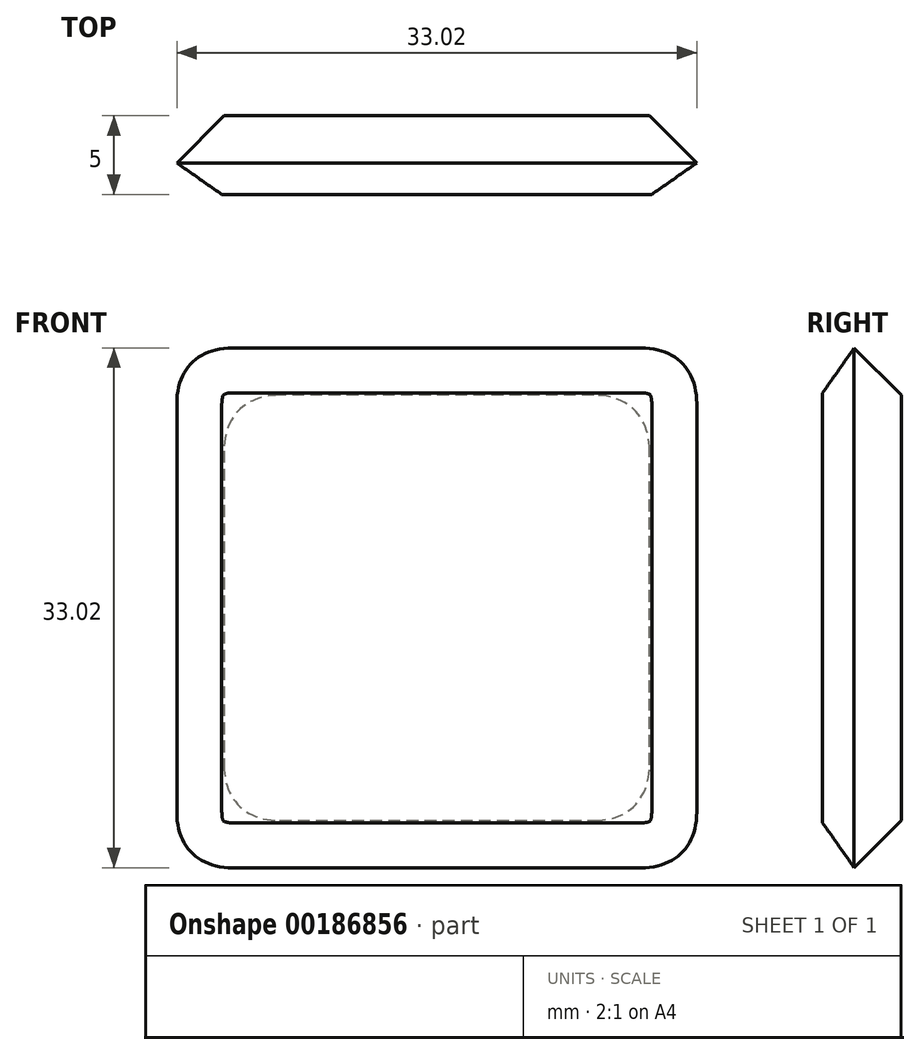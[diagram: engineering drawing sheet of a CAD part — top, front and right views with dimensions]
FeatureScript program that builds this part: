
annotation { "Feature Type Name" : "Feature", "Feature Type Description" : "" }
export const myFeature = defineFeature(function(context is Context, id is Id, definition is map)
    precondition{}
    {
        {
            var Q0;
            Q0=qCreatedBy(makeId("Front.planeOp"),FACE);
            var sketch = newSketch(context, id + "F0", { "sketchPlane" : qUnion([Q0])});
            skLineSegment(sketch, "E0.bottom", {"start": v(-16.51, 16.51) * mm, "end": v(16.51, 16.51) * mm});
            skLineSegment(sketch, "E0.top", {"start": v(-16.51, -16.51) * mm, "end": v(16.51, -16.51) * mm});
            skLineSegment(sketch, "E0.left", {"start": v(-16.51, 16.51) * mm, "end": v(-16.51, -16.51) * mm});
            skLineSegment(sketch, "E0.right", {"start": v(16.51, 16.51) * mm, "end": v(16.51, -16.51) * mm});
            skPoint(sketch, "E0.middle", {"position": v(0, 0) * mm});
            skSolve(sketch);
        }
        {
            var Q0;
            Q0=makeQuery(id+"F0.imprint","IMPRINT",FACE,{"disambiguationData":[TD([[makeQuery(id+"F0.imprint","IMPRINT",EDGE,{"derivedFrom":sQuery(id+"F0.wireOp",EDGE,"E0.bottom")}),-1.0]])]});
            extrude(context, id + "F1", {"entities" : qUnion([Q0]), "oppositeDirection" : true, "depth" : 3 * mm, "hasDraft" : true, "draftAngle" : 45 * degree, "draftPullDirection" : true});
        }
        {
            var Q0;
            Q0=makeQuery(id+"F1.opExtrude","SWEPT_EDGE",EDGE,{"disambiguationData":[OSD([sQuery(id+"F0.wireOp",EDGE,"E0.top"),sQuery(id+"F0.wireOp",EDGE,"E0.left")])]});
            var Q1;
            Q1=makeQuery(id+"F1.opExtrude","SWEPT_EDGE",EDGE,{"disambiguationData":[OSD([sQuery(id+"F0.wireOp",EDGE,"E0.bottom"),sQuery(id+"F0.wireOp",EDGE,"E0.left")])]});
            var Q2;
            Q2=makeQuery(id+"F1.opExtrude","SWEPT_EDGE",EDGE,{"disambiguationData":[OSD([sQuery(id+"F0.wireOp",EDGE,"E0.bottom"),sQuery(id+"F0.wireOp",EDGE,"E0.right")])]});
            var Q3;
            Q3=makeQuery(id+"F1.opExtrude","SWEPT_EDGE",EDGE,{"disambiguationData":[OSD([sQuery(id+"F0.wireOp",EDGE,"E0.top"),sQuery(id+"F0.wireOp",EDGE,"E0.right")])]});
            fillet(context, id + "F2", {"entities" : qUnion([Q0, Q1, Q2, Q3]), "radius" : 5 * mm, "tangentPropagation" : true, "allowEdgeOverflow" : false});
        }
        {
            var Q0;
            Q0=makeQuery(id+"F1.opExtrude","CAP_FACE",FACE,{"disambiguationData":[OSD([sQuery(id+"F0.wireOp",EDGE,"E0.bottom"),sQuery(id+"F0.wireOp",EDGE,"E0.top"),sQuery(id+"F0.wireOp",EDGE,"E0.left"),sQuery(id+"F0.wireOp",EDGE,"E0.right")])],"isStart":true});
            extrude(context, id + "F3", {"entities" : qUnion([Q0]), "operationType" : NewBodyOperationType.ADD, "depth" : 2 * mm, "hasDraft" : true, "draftAngle" : 55 * degree, "draftPullDirection" : true});
        }
    });
